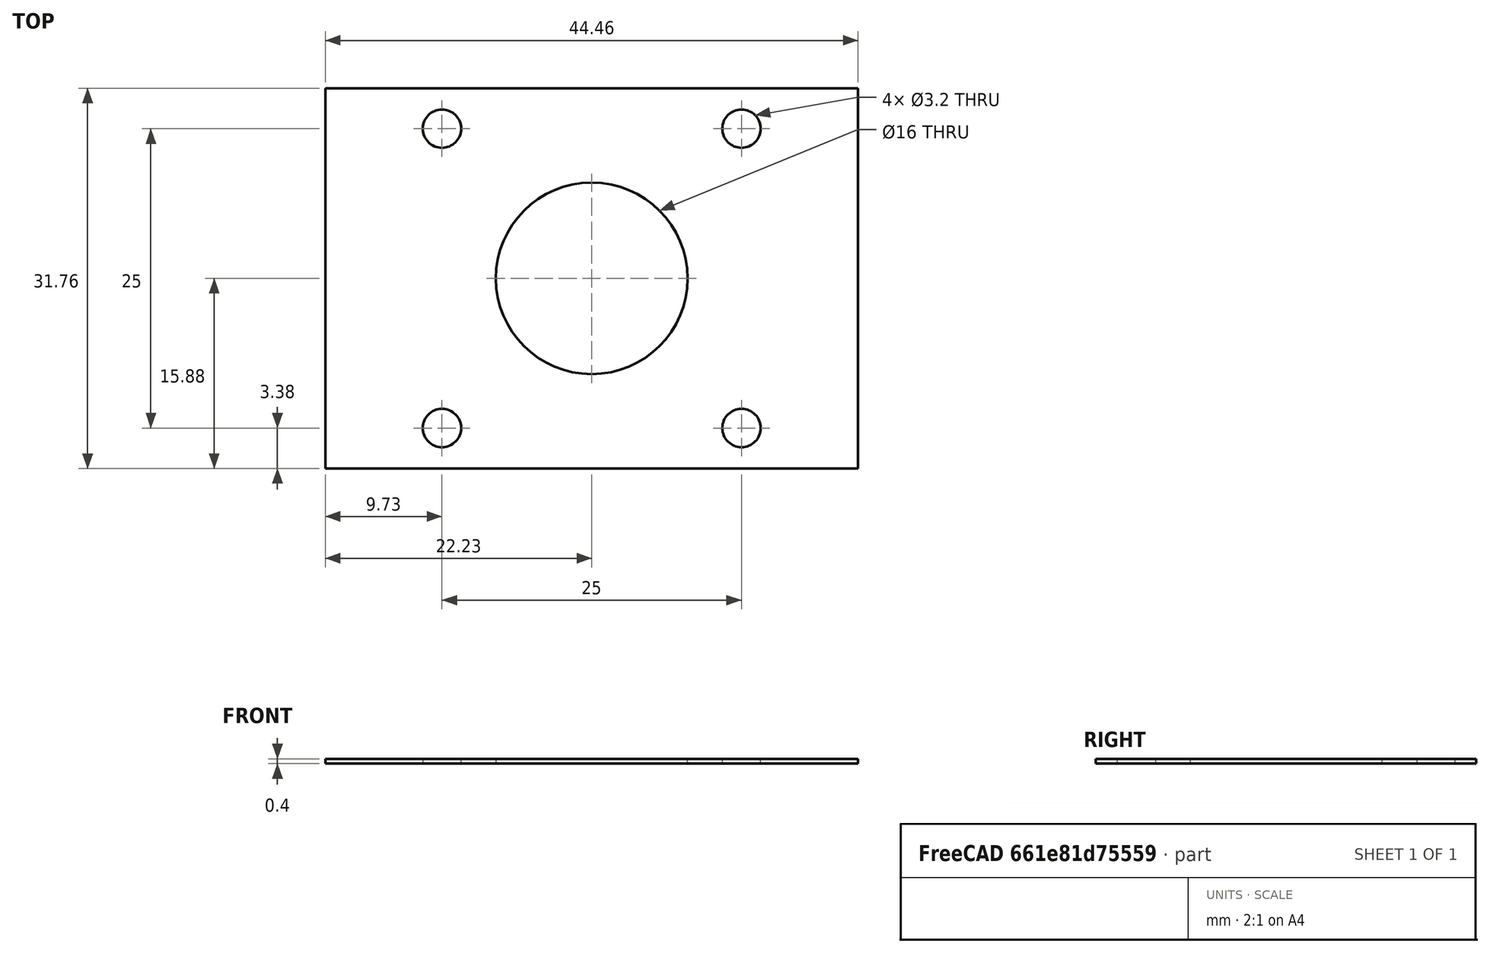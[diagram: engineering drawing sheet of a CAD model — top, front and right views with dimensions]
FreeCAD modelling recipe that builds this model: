
FCSTD DOCUMENT  (FreeCAD 0.20R29603 (Git))
Label: Upper Spacer
License: All rights reserved
LicenseURL: http://en.wikipedia.org/wiki/All_rights_reserved
objects: Sketcher::SketchObject×1, PartDesign::Pad×1, PartDesign::Body×1
note: 4 computed .brp shape members not serialized (recipe doc carries the construction recipe); baked Part::Feature solids carry a one-line shape summary decoded from their .brp

FEATURE [Sketcher::SketchObject] Sketch
  FullyConstrained = true
  MapMode = 5
  Support = -> [XY_Plane]
  sketch-geometry (15):
    g0: LineSegment StartX=-22.225 StartY=15.875 StartZ=0 EndX=-22.225 EndY=-15.875 EndZ=0
    g1: LineSegment StartX=-22.225 StartY=-15.875 StartZ=0 EndX=22.225 EndY=-15.875 EndZ=0
    g2: LineSegment StartX=22.225 StartY=-15.875 StartZ=0 EndX=22.225 EndY=15.875 EndZ=0
    g3: LineSegment StartX=22.225 StartY=15.875 StartZ=0 EndX=-22.225 EndY=15.875 EndZ=0
    g4: GeomPoint X=0 Y=0 Z=0
    g5: LineSegment StartX=-12.5 StartY=12.5 StartZ=0 EndX=-12.5 EndY=-12.5 EndZ=0
    g6: LineSegment StartX=-12.5 StartY=-12.5 StartZ=0 EndX=12.5 EndY=-12.5 EndZ=0
    g7: LineSegment StartX=12.5 StartY=-12.5 StartZ=0 EndX=12.5 EndY=12.5 EndZ=0
    g8: LineSegment StartX=12.5 StartY=12.5 StartZ=0 EndX=-12.5 EndY=12.5 EndZ=0
    g9: GeomPoint X=0 Y=0 Z=0
    g10: Circle CenterX=-12.5 CenterY=12.5 CenterZ=0 NormalX=0 NormalY=0 NormalZ=1 AngleXU=0 Radius=1.6
    g11: Circle CenterX=12.5 CenterY=12.5 CenterZ=0 NormalX=0 NormalY=0 NormalZ=1 AngleXU=0 Radius=1.6
    g12: Circle CenterX=12.5 CenterY=-12.5 CenterZ=0 NormalX=0 NormalY=0 NormalZ=1 AngleXU=0 Radius=1.6
    g13: Circle CenterX=-12.5 CenterY=-12.5 CenterZ=0 NormalX=0 NormalY=0 NormalZ=1 AngleXU=0 Radius=1.6
    g14: Circle CenterX=0 CenterY=0 CenterZ=0 NormalX=0 NormalY=0 NormalZ=1 AngleXU=0 Radius=8
  constraints (34):
    c: Coincident(g0,g1)
    c: Coincident(g1,g2)
    c: Coincident(g2,g3)
    c: Coincident(g3,g0)
    c: Horizontal(g1)
    c: Horizontal(g3)
    c: Vertical(g0)
    c: Vertical(g2)
    c: Symmetric(g1,g0,g4)
    c: Coincident(g5,g6)
    c: Coincident(g6,g7)
    c: Coincident(g7,g8)
    c: Coincident(g8,g5)
    c: Horizontal(g6)
    c: Horizontal(g8)
    c: Vertical(g5)
    c: Vertical(g7)
    c: Symmetric(g6,g5,g9)
    c: Coincident(g9,g-1)
    c: Coincident(g9,g4)
    c: DistanceY(g2,g2) = 31.75
    c: DistanceX(g3,g3) = 44.45
    c: Equal(g7,g8)
    c: DistanceX(g8,g8) = 25
    c: Coincident(g11,g7)
    c: Coincident(g12,g6)
    c: Coincident(g13,g5)
    c: Equal(g12,g13)
    c: Equal(g12,g10)
    c: Equal(g12,g11)
    c: Diameter(g12) = 3.2
    c: Coincident(g5,g10)
    c: Coincident(g14,g4)
    c: Diameter(g14) = 16
FEATURE [PartDesign::Pad] Pad
  Direction = (0,0,1)
  Length = 0.4
  Length2 = 10
  Profile = -> Sketch
  ReferenceAxis = -> Sketch [N_Axis]
  Type = 0
FEATURE [PartDesign::Body] Body
  Group = -> [Sketch,Pad]
  Origin = -> Origin
  Tip = -> Pad
